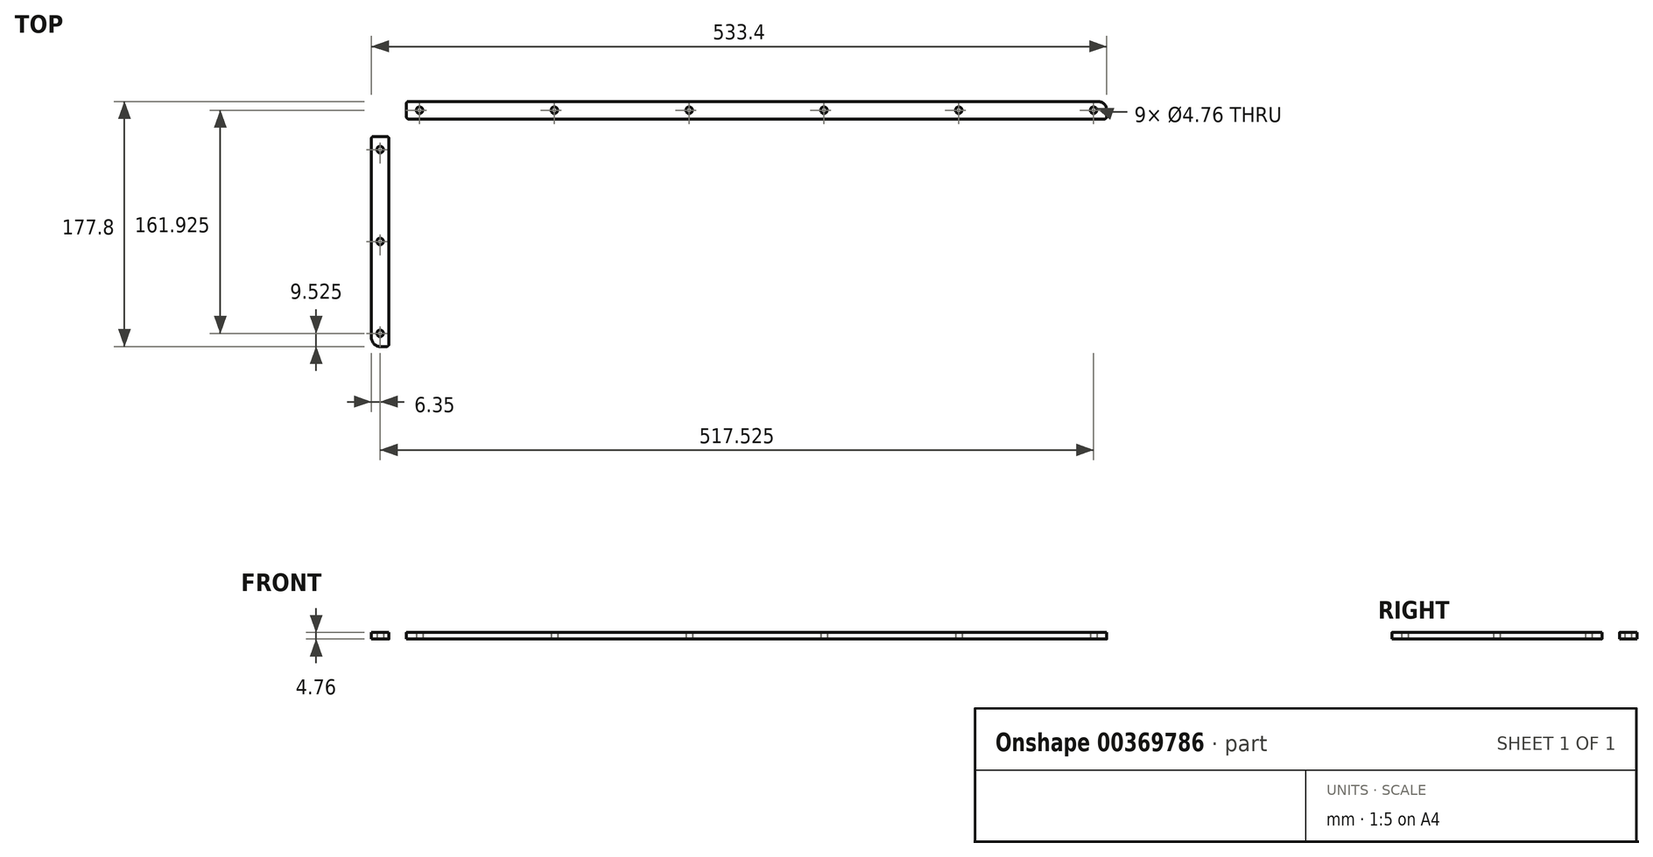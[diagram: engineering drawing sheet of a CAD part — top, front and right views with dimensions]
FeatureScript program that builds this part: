
annotation { "Feature Type Name" : "Feature", "Feature Type Description" : "" }
export const myFeature = defineFeature(function(context is Context, id is Id, definition is map)
    precondition{}
    {
        {
            var Q0;
            Q0=qCreatedBy(makeId("Top.planeOp"),FACE);
            var sketch = newSketch(context, id + "F0", { "sketchPlane" : qUnion([Q0])});
            skLineSegment(sketch, "E0.bottom", {"start": v(6.35, 0) * mm, "end": v(527.05, 0) * mm});
            skLineSegment(sketch, "E0.top", {"start": v(6.35, 177.8) * mm, "end": v(196.85, 177.8) * mm});
            skLineSegment(sketch, "E0.left", {"start": v(0, 6.35) * mm, "end": v(0, 171.45) * mm});
            skLineSegment(sketch, "E0.right", {"start": v(533.4, 6.35) * mm, "end": v(533.4, 171.45) * mm});
            skCircle(sketch, "E1", {"center": v(257.18, 93.66) * mm, "radius": 2.38 * mm});
            skCircle(sketch, "E2", {"center": v(257.18, 30.16) * mm, "radius": 2.38 * mm});
            skCircle(sketch, "E3", {"center": v(485.78, 93.66) * mm, "radius": 2.38 * mm});
            skCircle(sketch, "E4", {"center": v(485.78, 30.16) * mm, "radius": 2.38 * mm});
            skLineSegment(sketch, "E5", {"start": v(0, 165.1) * mm, "end": v(533.4, 165.1) * mm, "construction": true});
            skLineSegment(sketch, "E6.0", {"start": v(0, 152.4) * mm, "end": v(648.77, 152.4) * mm, "construction": true});
            skLineSegment(sketch, "E7.0", {"start": v(12.7, 0) * mm, "end": v(12.7, 177.8) * mm, "construction": true});
            skLineSegment(sketch, "E8.0", {"start": v(25.4, 0) * mm, "end": v(25.4, 177.8) * mm, "construction": true});
            skLineSegment(sketch, "E9.0", {"start": v(266.7, 177.8) * mm, "end": v(266.7, 267.26) * mm, "construction": true});
            skLineSegment(sketch, "E10.0", {"start": v(330.2, 184.15) * mm, "end": v(330.2, 203.2) * mm});
            skLineSegment(sketch, "E11.0", {"start": v(203.2, 184.15) * mm, "end": v(203.2, 203.2) * mm});
            skLineSegment(sketch, "E12.0", {"start": v(209.55, 209.55) * mm, "end": v(323.85, 209.55) * mm});
            skArc(sketch, "E13.filletArc", {"start": v(209.55, 209.55) * mm, "mid": v(205.06, 207.7) * mm, "end": v(203.2, 203.2) * mm});
            skLineSegment(sketch, "E14.trimOffspring", {"start": v(336.55, 177.8) * mm, "end": v(527.05, 177.8) * mm});
            skPoint(sketch, "E15.visualSharp", {"position": v(203.2, 177.8) * mm});
            skArc(sketch, "E15.filletArc", {"start": v(196.85, 177.8) * mm, "mid": v(201.34, 179.66) * mm, "end": v(203.2, 184.15) * mm});
            skArc(sketch, "E16.filletArc", {"start": v(330.2, 203.2) * mm, "mid": v(328.34, 207.7) * mm, "end": v(323.85, 209.55) * mm});
            skPoint(sketch, "E17.visualSharp", {"position": v(330.2, 177.8) * mm});
            skArc(sketch, "E17.filletArc", {"start": v(330.2, 184.15) * mm, "mid": v(332.06, 179.66) * mm, "end": v(336.55, 177.8) * mm});
            skCircle(sketch, "E18", {"center": v(239.71, 185.74) * mm, "radius": 2.38 * mm});
            skCircle(sketch, "E19", {"center": v(223.84, 195.26) * mm, "radius": 2.38 * mm});
            skCircle(sketch, "E20", {"center": v(309.56, 195.26) * mm, "radius": 2.38 * mm});
            skCircle(sketch, "E21", {"center": v(293.69, 185.74) * mm, "radius": 2.38 * mm});
            skLineSegment(sketch, "E22", {"start": v(239.71, 185.74) * mm, "end": v(293.69, 185.74) * mm, "construction": true});
            skLineSegment(sketch, "E23", {"start": v(309.56, 195.26) * mm, "end": v(223.84, 195.26) * mm, "construction": true});
            skPoint(sketch, "E24", {"position": v(266.7, 195.26) * mm});
            skPoint(sketch, "E25", {"position": v(266.7, 185.74) * mm});
            skPoint(sketch, "E26.visualSharp", {"position": v(0, 177.8) * mm});
            skArc(sketch, "E26.filletArc", {"start": v(6.35, 177.8) * mm, "mid": v(1.86, 175.94) * mm, "end": v(0, 171.45) * mm});
            skPoint(sketch, "E27.visualSharp", {"position": v(0, 0) * mm});
            skArc(sketch, "E27.filletArc", {"start": v(0, 6.35) * mm, "mid": v(1.86, 1.86) * mm, "end": v(6.35, 0) * mm});
            skPoint(sketch, "E28.visualSharp", {"position": v(533.4, 0) * mm});
            skArc(sketch, "E28.filletArc", {"start": v(527.05, 0) * mm, "mid": v(531.54, 1.86) * mm, "end": v(533.4, 6.35) * mm});
            skPoint(sketch, "E29.visualSharp", {"position": v(533.4, 177.8) * mm});
            skArc(sketch, "E29.filletArc", {"start": v(533.4, 171.45) * mm, "mid": v(531.54, 175.94) * mm, "end": v(527.05, 177.8) * mm});
            skCircle(sketch, "E30", {"center": v(6.35, 9.53) * mm, "radius": 2.38 * mm});
            skCircle(sketch, "E31", {"center": v(6.35, 76.2) * mm, "radius": 2.38 * mm});
            skCircle(sketch, "E32", {"center": v(6.35, 142.88) * mm, "radius": 2.38 * mm});
            skCircle(sketch, "E33", {"center": v(34.93, 171.45) * mm, "radius": 2.38 * mm});
            skCircle(sketch, "E34", {"center": v(132.72, 171.45) * mm, "radius": 2.38 * mm});
            skCircle(sketch, "E35", {"center": v(230.5, 171.45) * mm, "radius": 2.38 * mm});
            skCircle(sketch, "E36", {"center": v(328.3, 171.45) * mm, "radius": 2.38 * mm});
            skCircle(sketch, "E37", {"center": v(426.09, 171.45) * mm, "radius": 2.38 * mm});
            skCircle(sketch, "E38", {"center": v(523.88, 171.45) * mm, "radius": 2.38 * mm});
            skLineSegment(sketch, "E39", {"start": v(34.92, 171.45) * mm, "end": v(132.72, 171.45) * mm, "construction": true});
            skLineSegment(sketch, "E40", {"start": v(132.72, 171.45) * mm, "end": v(230.5, 171.45) * mm, "construction": true});
            skLineSegment(sketch, "E41", {"start": v(230.5, 171.45) * mm, "end": v(328.3, 171.45) * mm, "construction": true});
            skLineSegment(sketch, "E42", {"start": v(328.3, 171.45) * mm, "end": v(426.09, 171.45) * mm, "construction": true});
            skLineSegment(sketch, "E43", {"start": v(426.09, 171.45) * mm, "end": v(523.88, 171.45) * mm, "construction": true});
            skLineSegment(sketch, "E44", {"start": v(6.35, 142.88) * mm, "end": v(6.35, 76.2) * mm, "construction": true});
            skLineSegment(sketch, "E45", {"start": v(6.35, 76.2) * mm, "end": v(6.35, 9.53) * mm, "construction": true});
            skSolve(sketch);
        }
        {
            var Q0;
            Q0=qSketchRegion(id+"F0",true);
            extrude(context, id + "F1", {"entities" : qUnion([Q0]), "depth" : 4.76 * mm});
        }
        {
            var Q0;
            Q0=makeQuery(id+"F1.opExtrude","CAP_FACE",FACE,{"disambiguationData":[OSD([sQuery(id+"F0.wireOp",EDGE,"E0.bottom"),sQuery(id+"F0.wireOp",EDGE,"E0.top"),sQuery(id+"F0.wireOp",EDGE,"E0.left"),sQuery(id+"F0.wireOp",EDGE,"E0.right"),sQuery(id+"F0.wireOp",EDGE,"E1"),sQuery(id+"F0.wireOp",EDGE,"E2"),sQuery(id+"F0.wireOp",EDGE,"E3"),sQuery(id+"F0.wireOp",EDGE,"E4"),sQuery(id+"F0.wireOp",EDGE,"E10.0"),sQuery(id+"F0.wireOp",EDGE,"E11.0"),sQuery(id+"F0.wireOp",EDGE,"E12.0"),sQuery(id+"F0.wireOp",EDGE,"E13.filletArc"),sQuery(id+"F0.wireOp",EDGE,"E14.trimOffspring"),sQuery(id+"F0.wireOp",EDGE,"E15.filletArc"),sQuery(id+"F0.wireOp",EDGE,"E16.filletArc"),sQuery(id+"F0.wireOp",EDGE,"E17.filletArc"),sQuery(id+"F0.wireOp",EDGE,"E18"),sQuery(id+"F0.wireOp",EDGE,"E19"),sQuery(id+"F0.wireOp",EDGE,"E20"),sQuery(id+"F0.wireOp",EDGE,"E21"),sQuery(id+"F0.wireOp",EDGE,"E26.filletArc"),sQuery(id+"F0.wireOp",EDGE,"E27.filletArc"),sQuery(id+"F0.wireOp",EDGE,"E28.filletArc"),sQuery(id+"F0.wireOp",EDGE,"E29.filletArc"),sQuery(id+"F0.wireOp",EDGE,"E30"),sQuery(id+"F0.wireOp",EDGE,"E31"),sQuery(id+"F0.wireOp",EDGE,"E32"),sQuery(id+"F0.wireOp",EDGE,"E33"),sQuery(id+"F0.wireOp",EDGE,"E34"),sQuery(id+"F0.wireOp",EDGE,"E35"),sQuery(id+"F0.wireOp",EDGE,"E36"),sQuery(id+"F0.wireOp",EDGE,"E37"),sQuery(id+"F0.wireOp",EDGE,"E38")])],"isStart":false});
            var sketch = newSketch(context, id + "F2", { "sketchPlane" : qUnion([Q0])});
            skText(sketch, "E46", { "text": "STANLEY\nD-4550 & D-4551\nPARALLEL ARM\nPUSH SIDE\nTHIS SIDE LEFT HAND", "fontName": "NotoSansCJKjp-Regular.otf"});
            const initialGuessF2  = {"E46": [0.05559, 0.10161, 1, 0, 0.01089]};
            skSetInitialGuess(sketch, initialGuessF2);
            skSolve(sketch);
        }
        {
            var Q0;
            Q0=qSketchRegion(id+"F2",true);
            extrude(context, id + "F3", {"entities" : qUnion([Q0]), "operationType" : NewBodyOperationType.REMOVE, "oppositeDirection" : true, "depth" : 0.8 * mm});
        }
        {
            var Q0;
            {var subQ0=sQuery(id+"F0.wireOp",EDGE,"E37");var subQ1=sQuery(id+"F0.wireOp",EDGE,"E36");var subQ2=sQuery(id+"F0.wireOp",EDGE,"E33");var subQ3=sQuery(id+"F0.wireOp",EDGE,"E32");var subQ4=sQuery(id+"F0.wireOp",EDGE,"E31");var subQ5=sQuery(id+"F0.wireOp",EDGE,"E30");var subQ6=sQuery(id+"F0.wireOp",EDGE,"E29.filletArc");var subQ7=sQuery(id+"F0.wireOp",EDGE,"E28.filletArc");var subQ8=sQuery(id+"F0.wireOp",EDGE,"E21");var subQ9=sQuery(id+"F0.wireOp",EDGE,"E20");var subQ10=sQuery(id+"F0.wireOp",EDGE,"E19");var subQ11=sQuery(id+"F0.wireOp",EDGE,"E18");var subQ12=sQuery(id+"F0.wireOp",EDGE,"E17.filletArc");var subQ13=sQuery(id+"F0.wireOp",EDGE,"E16.filletArc");var subQ14=sQuery(id+"F0.wireOp",EDGE,"E15.filletArc");var subQ15=sQuery(id+"F0.wireOp",EDGE,"E14.trimOffspring");var subQ16=sQuery(id+"F0.wireOp",EDGE,"E13.filletArc");var subQ17=sQuery(id+"F0.wireOp",EDGE,"E0.left");var subQ18=sQuery(id+"F0.wireOp",EDGE,"E0.top");var subQ19=sQuery(id+"F0.wireOp",EDGE,"E0.bottom");var subQ20=sQuery(id+"F0.wireOp",EDGE,"E12.0");var subQ21=sQuery(id+"F0.wireOp",EDGE,"E38");var subQ22=sQuery(id+"F0.wireOp",EDGE,"E0.right");var subQ23=sQuery(id+"F0.wireOp",EDGE,"E11.0");var subQ24=sQuery(id+"F0.wireOp",EDGE,"E1");var subQ25=sQuery(id+"F0.wireOp",EDGE,"E2");var subQ26=sQuery(id+"F0.wireOp",EDGE,"E3");var subQ27=sQuery(id+"F0.wireOp",EDGE,"E4");var subQ28=sQuery(id+"F0.wireOp",EDGE,"E10.0");var subQ29=sQuery(id+"F0.wireOp",EDGE,"E34");var subQ30=sQuery(id+"F0.wireOp",EDGE,"E26.filletArc");var subQ31=sQuery(id+"F0.wireOp",EDGE,"E35");var subQ32=sQuery(id+"F0.wireOp",EDGE,"E27.filletArc");Q0=makeQuery(id+"F3.boolean.opBoolean","SPLIT",FACE,{"disambiguationData":[TD([makeQuery(id+"F1.opExtrude","SWEPT_FACE",FACE,{"disambiguationData":[OSD([subQ19])]})])],"derivedFrom":makeQuery(id+"F1.opExtrude","CAP_FACE",FACE,{"disambiguationData":[OSD([subQ19,subQ18,subQ17,subQ22,subQ24,subQ25,subQ26,subQ27,subQ28,subQ23,subQ20,subQ16,subQ15,subQ14,subQ13,subQ12,subQ11,subQ10,subQ9,subQ8,subQ30,subQ32,subQ7,subQ6,subQ5,subQ4,subQ3,subQ2,subQ29,subQ31,subQ1,subQ0,subQ21])],"isStart":false})});}
            var sketch = newSketch(context, id + "F4", { "sketchPlane" : qUnion([Q0])});
            skLineSegment(sketch, "E47.bottom", {"start": v(195.48, 216.28) * mm, "end": v(344.34, 216.28) * mm});
            skLineSegment(sketch, "E47.top", {"start": v(195.48, 177.8) * mm, "end": v(344.34, 177.8) * mm});
            skLineSegment(sketch, "E47.left", {"start": v(195.48, 216.28) * mm, "end": v(195.48, 177.8) * mm});
            skLineSegment(sketch, "E47.right", {"start": v(344.34, 216.28) * mm, "end": v(344.34, 177.8) * mm});
            skLineSegment(sketch, "E48.bottom", {"start": v(-12.66, 185.6) * mm, "end": v(25.4, 185.6) * mm});
            skLineSegment(sketch, "E48.top", {"start": v(-12.66, 152.4) * mm, "end": v(25.4, 152.4) * mm});
            skLineSegment(sketch, "E48.left", {"start": v(-12.66, 185.6) * mm, "end": v(-12.66, 152.4) * mm});
            skLineSegment(sketch, "E48.right", {"start": v(25.4, 185.6) * mm, "end": v(25.4, 152.4) * mm});
            skLineSegment(sketch, "E49.bottom", {"start": v(12.7, 165.1) * mm, "end": v(533.4, 165.1) * mm});
            skLineSegment(sketch, "E49.top", {"start": v(12.7, 0) * mm, "end": v(533.4, 0) * mm});
            skLineSegment(sketch, "E49.left", {"start": v(12.7, 165.1) * mm, "end": v(12.7, 0) * mm});
            skLineSegment(sketch, "E49.right", {"start": v(533.4, 165.1) * mm, "end": v(533.4, 0) * mm});
            skPoint(sketch, "E50", {"position": v(34.93, 171.45) * mm});
            skPoint(sketch, "E51", {"position": v(6.35, 142.88) * mm});
            skSolve(sketch);
        }
        {
            var Q0;
            Q0 = qSketchRegion(id + "F4", true);
            extrude(context, id + "F5", {"entities" : qUnion([Q0]), "operationType" : NewBodyOperationType.REMOVE, "endBound" : BoundingType.THROUGH_ALL, "oppositeDirection" : true, "depth" : 25.4 * mm});
        }
        {
            var Q0;
            {var subQ0=sQuery(id+"F0.wireOp",EDGE,"E30");var subQ2=sQuery(id+"F0.wireOp",EDGE,"E0.left");var subQ4=sQuery(id+"F0.wireOp",EDGE,"E27.filletArc");var subQ6=sQuery(id+"F0.wireOp",EDGE,"E0.bottom");var subQ7=makeQuery(id+"F1.opExtrude","SWEPT_FACE",FACE,{"disambiguationData":[OSD([subQ6])]});var subQ8=sQuery(id+"F0.wireOp",EDGE,"E31");var subQ10=sQuery(id+"F0.wireOp",EDGE,"E32");var subQ12=sQuery(id+"F0.wireOp",EDGE,"E37");var subQ13=sQuery(id+"F0.wireOp",EDGE,"E36");var subQ14=sQuery(id+"F0.wireOp",EDGE,"E33");var subQ15=sQuery(id+"F0.wireOp",EDGE,"E29.filletArc");var subQ16=sQuery(id+"F0.wireOp",EDGE,"E28.filletArc");var subQ17=sQuery(id+"F0.wireOp",EDGE,"E21");var subQ18=sQuery(id+"F0.wireOp",EDGE,"E20");var subQ19=sQuery(id+"F0.wireOp",EDGE,"E19");var subQ20=sQuery(id+"F0.wireOp",EDGE,"E18");var subQ21=sQuery(id+"F0.wireOp",EDGE,"E17.filletArc");var subQ22=sQuery(id+"F0.wireOp",EDGE,"E16.filletArc");var subQ23=sQuery(id+"F0.wireOp",EDGE,"E15.filletArc");var subQ24=sQuery(id+"F0.wireOp",EDGE,"E14.trimOffspring");var subQ25=sQuery(id+"F0.wireOp",EDGE,"E13.filletArc");var subQ26=sQuery(id+"F0.wireOp",EDGE,"E0.top");var subQ27=sQuery(id+"F0.wireOp",EDGE,"E12.0");var subQ28=sQuery(id+"F0.wireOp",EDGE,"E38");var subQ29=sQuery(id+"F0.wireOp",EDGE,"E0.right");var subQ30=sQuery(id+"F0.wireOp",EDGE,"E11.0");var subQ31=sQuery(id+"F0.wireOp",EDGE,"E1");var subQ32=sQuery(id+"F0.wireOp",EDGE,"E2");var subQ33=sQuery(id+"F0.wireOp",EDGE,"E3");var subQ34=sQuery(id+"F0.wireOp",EDGE,"E4");var subQ35=sQuery(id+"F0.wireOp",EDGE,"E10.0");var subQ36=sQuery(id+"F0.wireOp",EDGE,"E34");var subQ37=sQuery(id+"F0.wireOp",EDGE,"E26.filletArc");var subQ38=sQuery(id+"F0.wireOp",EDGE,"E35");Q0=makeQuery(id+"F5.boolean.opBoolean","SPLIT",FACE,{"disambiguationData":[TD([subQ7])],"derivedFrom":makeQuery(id+"F3.boolean.opBoolean","SPLIT",FACE,{"disambiguationData":[TD([subQ7])],"derivedFrom":makeQuery(id+"F1.opExtrude","CAP_FACE",FACE,{"disambiguationData":[OSD([subQ6,subQ26,subQ2,subQ29,subQ31,subQ32,subQ33,subQ34,subQ35,subQ30,subQ27,subQ25,subQ24,subQ23,subQ22,subQ21,subQ20,subQ19,subQ18,subQ17,subQ37,subQ4,subQ16,subQ15,subQ0,subQ8,subQ10,subQ14,subQ36,subQ38,subQ13,subQ12,subQ28])],"isStart":false})})});}
            var sketch = newSketch(context, id + "F6", { "sketchPlane" : qUnion([Q0])});
            skLineSegment(sketch, "E52.0", {"start": v(12.7, 152.4) * mm, "end": v(12.7, 150.81) * mm});
            skLineSegment(sketch, "E53.0", {"start": v(0, 152.4) * mm, "end": v(1.59, 152.4) * mm});
            skLineSegment(sketch, "E54.0", {"start": v(0, 150.81) * mm, "end": v(0, 152.4) * mm});
            skLineSegment(sketch, "E55.0", {"start": v(11.11, 0) * mm, "end": v(12.7, 0) * mm});
            skPoint(sketch, "E56.visualSharp", {"position": v(0, 152.4) * mm});
            skArc(sketch, "E56.filletArc", {"start": v(1.59, 152.4) * mm, "mid": v(0.46, 151.94) * mm, "end": v(0, 150.81) * mm});
            skPoint(sketch, "E57.visualSharp", {"position": v(12.7, 152.4) * mm});
            skArc(sketch, "E57.filletArc", {"start": v(12.7, 150.81) * mm, "mid": v(12.24, 151.94) * mm, "end": v(11.11, 152.4) * mm});
            skPoint(sketch, "E58.visualSharp", {"position": v(12.7, 0) * mm});
            skArc(sketch, "E58.filletArc", {"start": v(11.11, 0) * mm, "mid": v(12.24, 0.46) * mm, "end": v(12.7, 1.59) * mm});
            skPoint(sketch, "E59.visualSharp", {"position": v(25.4, 177.8) * mm});
            skArc(sketch, "E59.filletArc", {"start": v(26.99, 177.8) * mm, "mid": v(25.86, 177.34) * mm, "end": v(25.4, 176.21) * mm});
            skPoint(sketch, "E60.visualSharp", {"position": v(25.4, 165.1) * mm});
            skArc(sketch, "E60.filletArc", {"start": v(25.4, 166.69) * mm, "mid": v(25.86, 165.56) * mm, "end": v(26.99, 165.1) * mm});
            skPoint(sketch, "E61.visualSharp", {"position": v(533.4, 165.1) * mm});
            skArc(sketch, "E61.filletArc", {"start": v(531.81, 165.1) * mm, "mid": v(532.94, 165.56) * mm, "end": v(533.4, 166.69) * mm});
            skLineSegment(sketch, "E62.0", {"start": v(533.4, 165.1) * mm, "end": v(533.4, 166.69) * mm});
            skLineSegment(sketch, "E62.1", {"start": v(25.4, 165.1) * mm, "end": v(26.99, 165.1) * mm});
            skLineSegment(sketch, "E63.trimOffspring", {"start": v(531.81, 165.1) * mm, "end": v(533.4, 165.1) * mm});
            skLineSegment(sketch, "E64.0", {"start": v(25.4, 177.8) * mm, "end": v(25.4, 176.21) * mm});
            skLineSegment(sketch, "E64.1", {"start": v(25.4, 177.8) * mm, "end": v(26.99, 177.8) * mm});
            skLineSegment(sketch, "E65.trimOffspring", {"start": v(25.4, 166.69) * mm, "end": v(25.4, 165.1) * mm});
            skLineSegment(sketch, "E66.trimOffspring", {"start": v(12.7, 1.59) * mm, "end": v(12.7, 0) * mm});
            skLineSegment(sketch, "E67.trimOffspring", {"start": v(11.11, 152.4) * mm, "end": v(12.7, 152.4) * mm});
            skSolve(sketch);
        }
        {
            var Q0;
            Q0 = qSketchRegion(id + "F6", true);
            extrude(context, id + "F7", {"entities" : qUnion([Q0]), "operationType" : NewBodyOperationType.REMOVE, "endBound" : BoundingType.UP_TO_NEXT, "oppositeDirection" : true, "depth" : 25.4 * mm});
        }
    });
